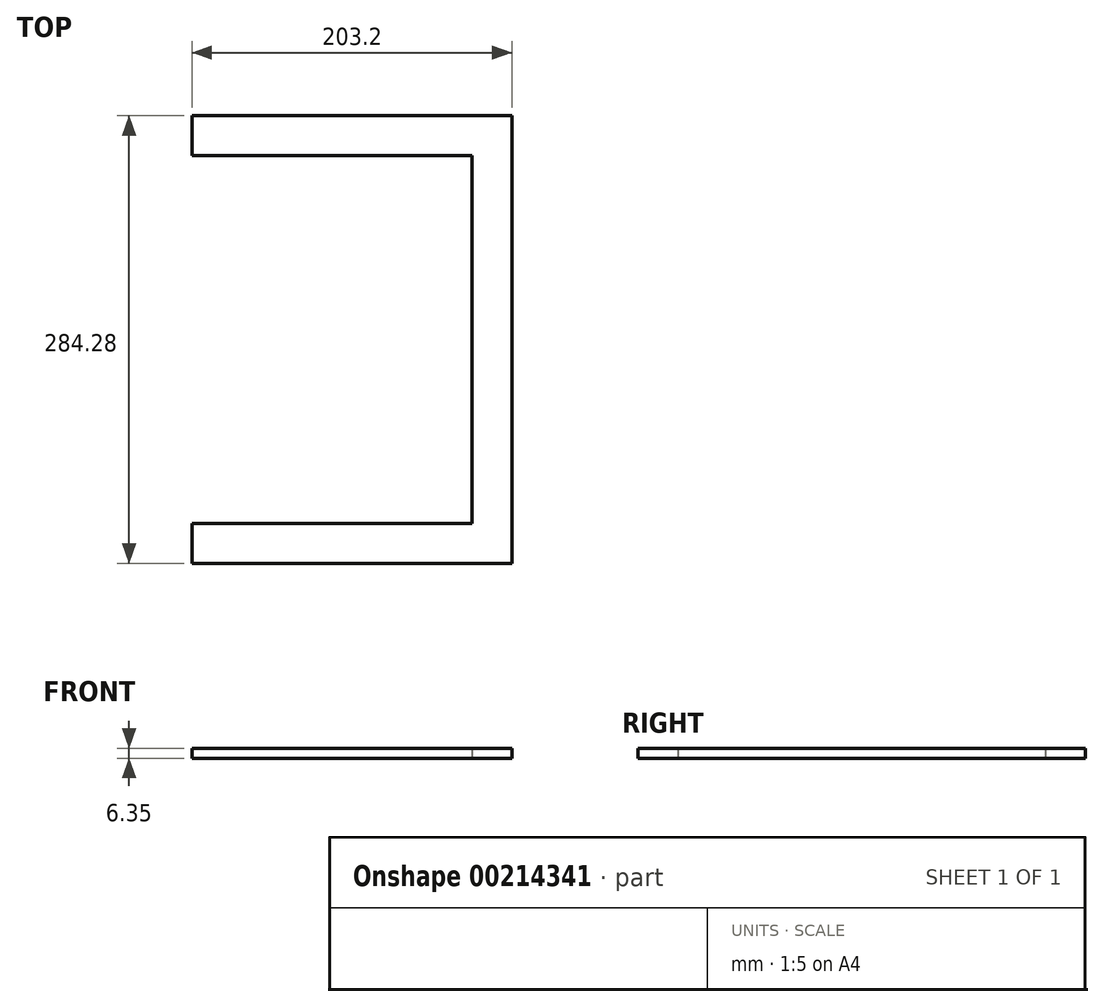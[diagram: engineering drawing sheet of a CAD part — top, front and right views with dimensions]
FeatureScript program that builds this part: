
annotation { "Feature Type Name" : "Feature", "Feature Type Description" : "" }
export const myFeature = defineFeature(function(context is Context, id is Id, definition is map)
    precondition{}
    {
        {
            var Q0;
            Q0=qCreatedBy(makeId("Top.planeOp"),FACE);
            var sketch = newSketch(context, id + "F0", { "sketchPlane" : qUnion([Q0])});
            skLineSegment(sketch, "E0.bottom", {"start": v(76.2, -116.74) * mm, "end": v(-76.2, -116.74) * mm});
            skLineSegment(sketch, "E0.top", {"start": v(76.2, 116.74) * mm, "end": v(-76.2, 116.74) * mm});
            skLineSegment(sketch, "E0.left", {"start": v(76.2, -116.74) * mm, "end": v(76.2, 116.74) * mm});
            skLineSegment(sketch, "E0.right", {"start": v(-76.2, -116.74) * mm, "end": v(-76.2, 116.74) * mm});
            skPoint(sketch, "E0.middle", {"position": v(0, 0) * mm});
            skLineSegment(sketch, "E1.0", {"start": v(101.6, 142.14) * mm, "end": v(-101.6, 142.14) * mm});
            skLineSegment(sketch, "E1.1", {"start": v(101.6, -142.14) * mm, "end": v(101.6, 142.14) * mm});
            skLineSegment(sketch, "E1.2", {"start": v(101.6, -142.14) * mm, "end": v(-101.6, -142.14) * mm});
            skLineSegment(sketch, "E1.3", {"start": v(-101.6, -142.14) * mm, "end": v(-101.6, -116.74) * mm});
            skLineSegment(sketch, "E2", {"start": v(-76.2, 116.74) * mm, "end": v(-101.6, 116.74) * mm});
            skLineSegment(sketch, "E3", {"start": v(-76.2, -116.74) * mm, "end": v(-101.6, -116.74) * mm});
            skLineSegment(sketch, "E4.trimOffspring", {"start": v(-101.6, 116.74) * mm, "end": v(-101.6, 142.14) * mm});
            skLineSegment(sketch, "E5", {"start": v(76.2, 116.74) * mm, "end": v(101.6, 116.74) * mm});
            skLineSegment(sketch, "E6", {"start": v(76.2, -116.74) * mm, "end": v(101.6, -116.74) * mm});
            skLineSegment(sketch, "E7", {"start": v(88.9, 116.74) * mm, "end": v(88.9, -116.74) * mm});
            skSolve(sketch);
        }
        {
            var Q0;
            Q0=makeQuery(id+"F0.imprint","IMPRINT",FACE,{"disambiguationData":[TD([[makeQuery(id+"F0.imprint","IMPRINT",EDGE,{"derivedFrom":sQuery(id+"F0.wireOp",EDGE,"E0.bottom")}),1.0]])]});
            var Q1;
            {var subQ0=sQuery(id+"F0.wireOp",EDGE,"SyIENNwF-CHkI-if3g-Oxzw-q1lJXSxW9fIR");Q1=makeQuery(id+"F0.imprint","IMPRINT",FACE,{"disambiguationData":[TD([[makeQuery(id+"F0.imprint","IMPRINT",EDGE,{"derivedFrom":subQ0}),-1.0]])]});}
            var Q2;
            Q2=makeQuery(id+"F0.imprint","IMPRINT",FACE,{"disambiguationData":[TD([[makeQuery(id+"F0.imprint","IMPRINT",EDGE,{"derivedFrom":sQuery(id+"F0.wireOp",EDGE,"E0.top")}),-1.0]])]});
            var Q3;
            {var subQ5=sQuery(id+"F0.wireOp",EDGE,"E7");Q3=makeQuery(id+"F0.imprint","IMPRINT",FACE,{"disambiguationData":[TD([[makeQuery(id+"F0.imprint","IMPRINT",EDGE,{"derivedFrom":subQ5}),1.0]])]});}
            var Q4;
            {var subQ0=sQuery(id+"F0.wireOp",EDGE,"E0.left");Q4=makeQuery(id+"F0.imprint","IMPRINT",FACE,{"disambiguationData":[TD([[makeQuery(id+"F0.imprint","IMPRINT",EDGE,{"derivedFrom":subQ0}),-1.0]])]});}
            extrude(context, id + "F1", {"entities" : qUnion([Q0, Q1, Q2, Q3, Q4]), "depth" : 6.35 * mm});
        }
    });
